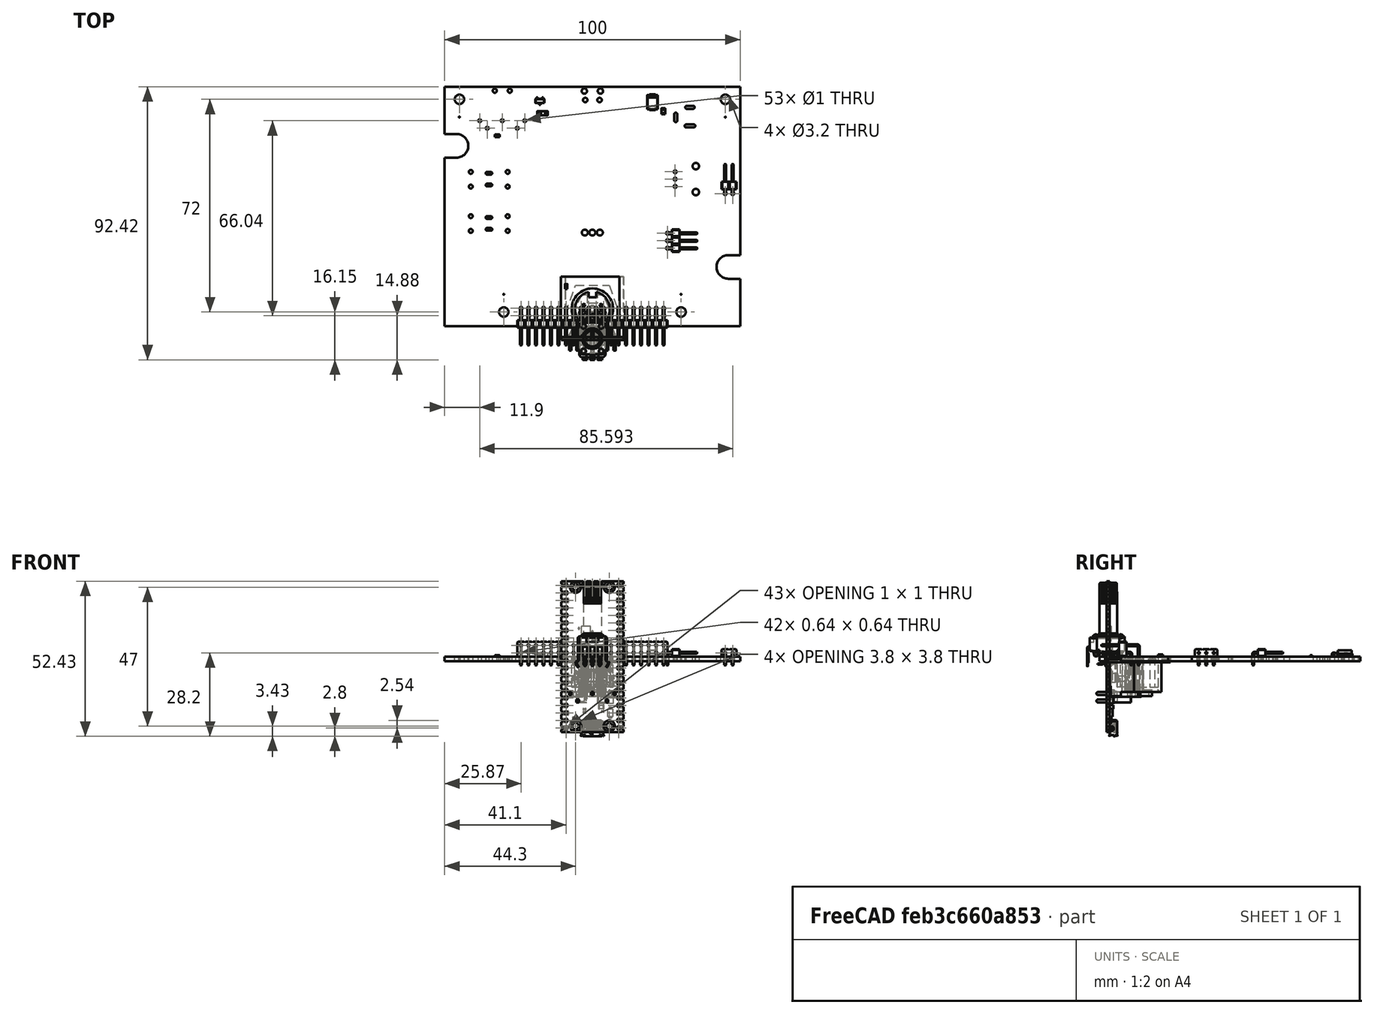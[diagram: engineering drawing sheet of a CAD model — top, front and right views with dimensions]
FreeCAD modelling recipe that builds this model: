
FCSTD DOCUMENT  (FreeCAD 0.21R33675 (Git))
Label: touch_keyboard_pcb
License: All rights reserved
LicenseURL: http://en.wikipedia.org/wiki/All_rights_reserved
objects: Part::Feature×161, App::Link×58, App::Part×42, PartDesign::CoordinateSystem×5, Sketcher::SketchObject×1
note: 167 computed .brp shape members not serialized (recipe doc carries the construction recipe); baked Part::Feature solids carry a one-line shape summary decoded from their .brp

FEATURE [PartDesign::CoordinateSystem] Local_CS_1056
  AttacherType = Attacher::AttachEngine3D
  MapMode = 2
  Support = -> [X_Axis001]
FEATURE [Part::Feature] Pcb_1056
  Placement = pos=(-142.24,138.54,0) rot=(0,0,1;0rad)
  shape: bbox 100 x 88.27 x 1.6 mm, 143 faces, 2 solids (baked)
FEATURE [Sketcher::SketchObject] PCB_Sketch_1056
  FullyConstrained = false
  sketch-geometry (16):
    g0: LineSegment StartX=46 StartY=20.27 StartZ=0 EndX=50 EndY=20.27 EndZ=0
    g1: LineSegment StartX=50 StartY=28.27 StartZ=0 EndX=46 EndY=28.27 EndZ=0
    g2: LineSegment StartX=-50 StartY=4.27 StartZ=0 EndX=-50 EndY=61.27 EndZ=0
    g3: LineSegment StartX=50 StartY=20.27 StartZ=0 EndX=50 EndY=4.27 EndZ=0
    g4: LineSegment StartX=50 StartY=85.27 StartZ=0 EndX=50 EndY=28.27 EndZ=0
    g5: LineSegment StartX=50 StartY=4.27 StartZ=0 EndX=-50 EndY=4.27 EndZ=0
    g6: LineSegment StartX=-50 StartY=85.27 StartZ=0 EndX=50 EndY=85.27 EndZ=0
    g7: LineSegment StartX=-46 StartY=69.27 StartZ=0 EndX=-50 EndY=69.27 EndZ=0
    g8: LineSegment StartX=-50 StartY=69.27 StartZ=0 EndX=-50 EndY=85.27 EndZ=0
    g9: LineSegment StartX=-50 StartY=61.27 StartZ=0 EndX=-46 EndY=61.27 EndZ=0
    g10: LineSegment StartX=-3 StartY=3 StartZ=0 EndX=3 EndY=3 EndZ=0
    g11: LineSegment StartX=3 StartY=3 StartZ=0 EndX=3 EndY=-3 EndZ=0
    g12: LineSegment StartX=3 StartY=-3 StartZ=0 EndX=-3 EndY=-3 EndZ=0
    g13: LineSegment StartX=-3 StartY=-3 StartZ=0 EndX=-3 EndY=3 EndZ=0
    g14: ArcOfCircle CenterX=-46 CenterY=65.27 CenterZ=0 NormalX=0 NormalY=0 NormalZ=-1 AngleXU=1.5708 Radius=4 StartAngle=0 EndAngle=3.14159
    g15: ArcOfCircle CenterX=46 CenterY=24.27 CenterZ=0 NormalX=0 NormalY=0 NormalZ=-1 AngleXU=-1.5708 Radius=4 StartAngle=0 EndAngle=3.14159
  constraints (16):
    c: Coincident(g2,g5)
    c: Coincident(g2,g9)
    c: Coincident(g7,g8)
    c: Coincident(g6,g8)
    c: Coincident(g9,g14)
    c: Coincident(g7,g14)
    c: Coincident(g12,g13)
    c: Coincident(g10,g13)
    c: Coincident(g11,g12)
    c: Coincident(g10,g11)
    c: Coincident(g0,g15)
    c: Coincident(g1,g15)
    c: Coincident(g3,g5)
    c: Coincident(g0,g3)
    c: Coincident(g1,g4)
    c: Coincident(g4,g6)
FEATURE [App::Part] Board_Geoms_1056
  Group = -> [Pcb_1056,PCB_Sketch_1056]
  Origin = -> Origin
FEATURE [Part::Feature] Shape  label="R33_R_0603_1608Metric_b52117b7a5b0"
  Placement = pos=(-32.195,68.69,0) rot=(0,0,1;0rad)
  shape: bbox 1.6 x 0.8 x 0.45 mm, 26 faces (baked)
FEATURE [Part::Feature] Shape001  label="C5_C_0603_1608Metric_656f8ebd2c8c"
  Placement = pos=(-8.89,17.65,0) rot=(0,0,-1;1.5708rad)
  shape: bbox 0.8 x 1.6 x 0.8 mm, 28 faces (baked)
FEATURE [App::Link] C5_C_0603_1608Metric_656f8ebd2c8c_ln_  label="C1_C_0603_1608Metric_563ebdbfda79"
  LinkPlacement = pos=(-19.05,17.65,0) rot=(0,0,-1;1.5708rad)
  LinkedObject = -> Shape001
  Placement = pos=(-19.05,17.65,0) rot=(0,0,-1;1.5708rad)
FEATURE [App::Link] R33_R_0603_1608Metric_b52117b7a5b0_ln_  label="R26_R_0603_1608Metric_01f404f3ffb8"
  LinkPlacement = pos=(11.43,13.89,0) rot=(0,0,-1;1.5708rad)
  LinkedObject = -> Shape
  Placement = pos=(11.43,13.89,0) rot=(0,0,-1;1.5708rad)
FEATURE [App::Link] R33_R_0603_1608Metric_b52117b7a5b0_ln_001  label="R29_R_0603_1608Metric_6abfc73d4d60"
  LinkPlacement = pos=(16.51,21.51,0) rot=(0,0,1;1.5708rad)
  LinkedObject = -> Shape
  Placement = pos=(16.51,21.51,0) rot=(0,0,1;1.5708rad)
FEATURE [App::Link] R33_R_0603_1608Metric_b52117b7a5b0_ln_002  label="R18_R_0603_1608Metric_edc7eae86286"
  LinkPlacement = pos=(1.27,13.89,0) rot=(0,0,-1;1.5708rad)
  LinkedObject = -> Shape
  Placement = pos=(1.27,13.89,0) rot=(0,0,-1;1.5708rad)
FEATURE [Part::Feature] Shape002  label="C18_C_0805_2012Metric_1ea8b0f87ad5"
  Placement = pos=(24,76.95,0) rot=(0,0,-1;1.5708rad)
  shape: bbox 1.25 x 2 x 1.25 mm, 28 faces (baked)
FEATURE [App::Link] R33_R_0603_1608Metric_b52117b7a5b0_ln_003  label="R8_R_0603_1608Metric_bf92398081f5"
  LinkPlacement = pos=(-11.43,13.89,0) rot=(0,0,-1;1.5708rad)
  LinkedObject = -> Shape
  Placement = pos=(-11.43,13.89,0) rot=(0,0,-1;1.5708rad)
FEATURE [App::Link] R33_R_0603_1608Metric_b52117b7a5b0_ln_004  label="R13_R_0603_1608Metric_2dbb6f5059f9"
  LinkPlacement = pos=(-3.81,21.51,0) rot=(0,0,1;1.5708rad)
  LinkedObject = -> Shape
  Placement = pos=(-3.81,21.51,0) rot=(0,0,1;1.5708rad)
FEATURE [App::Link] R33_R_0603_1608Metric_b52117b7a5b0_ln_005  label="R35_R_0603_1608Metric_a618b7082673"
  LinkPlacement = pos=(-15.685,83.93,0) rot=(0,0,1;3.14159rad)
  LinkedObject = -> Shape
  Placement = pos=(-15.685,83.93,0) rot=(0,0,1;3.14159rad)
FEATURE [App::Link] R33_R_0603_1608Metric_b52117b7a5b0_ln_006  label="R17_R_0603_1608Metric_51bdb2eb4169"
  LinkPlacement = pos=(1.27,21.51,0) rot=(0,0,1;1.5708rad)
  LinkedObject = -> Shape
  Placement = pos=(1.27,21.51,0) rot=(0,0,1;1.5708rad)
FEATURE [Part::Feature] Part__Feature  label="PCB, Raspberry Pi Pico-R3"
  shape: bbox 21 x 1 x 51 mm, 416 faces (baked)
FEATURE [Part::Feature] Part__Feature001  label="MicroUSB Port, Raspberry Pi Pico-R3"
  Placement = pos=(0,0.5,-24.35) rot=(0,1,0;3.14159rad)
  shape: bbox 7.999 x 2.949 x 5.461 mm, 809 faces (baked)
FEATURE [Part::Feature] Part__Feature002  label="MicroUSB Port, Raspberry Pi Pico-R004"
  Placement = pos=(0,0.5,-24.35) rot=(0,1,0;3.14159rad)
  shape: bbox 6.982 x 2.155 x 3.937 mm, 206 faces (baked)
FEATURE [Part::Feature] Part__Feature003  label="MicroUSB Port, Raspberry Pi Pico-R005"
  Placement = pos=(0,0.5,-24.35) rot=(0,1,0;3.14159rad)
  shape: bbox 0.37 x 1.716 x 4 mm, 43 faces (baked)
FEATURE [Part::Feature] Part__Feature004  label="MicroUSB Port, Raspberry Pi Pico-R006"
  Placement = pos=(0,0.5,-24.35) rot=(0,1,0;3.14159rad)
  shape: bbox 0.37 x 1.716 x 4 mm, 43 faces (baked)
FEATURE [Part::Feature] Part__Feature005  label="MicroUSB Port, Raspberry Pi Pico-R007"
  Placement = pos=(0,0.5,-24.35) rot=(0,1,0;3.14159rad)
  shape: bbox 0.37 x 1.716 x 4 mm, 43 faces (baked)
FEATURE [Part::Feature] Part__Feature006  label="MicroUSB Port, Raspberry Pi Pico-R008"
  Placement = pos=(0,0.5,-24.35) rot=(0,1,0;3.14159rad)
  shape: bbox 0.37 x 1.716 x 4 mm, 43 faces (baked)
FEATURE [Part::Feature] Part__Feature007  label="MicroUSB Port, Raspberry Pi Pico-R009"
  Placement = pos=(0,0.5,-24.35) rot=(0,1,0;3.14159rad)
  shape: bbox 0.37 x 1.716 x 4 mm, 43 faces (baked)
FEATURE [App::Part] MicroUSB_Port__Raspberry_Pi_Pico_R3  label="MicroUSB Port, Raspberry Pi Pico-R010"
  Group = -> [Part__Feature001,Part__Feature002,Part__Feature003,Part__Feature004,Part__Feature005,Part__Feature006,Part__Feature007]
  Origin = -> Origin008
FEATURE [Part::Feature] Part__Feature008  label="RP2040 Microcontroller, Raspberry Pi Pico-R3"
  Placement = pos=(0,0.5,0.5) rot=(0,0,1;0rad)
  shape: bbox 7 x 0.9 x 7 mm, 6 faces (baked)
FEATURE [Part::Feature] Part__Feature009  label="SW1, Tact Switch, Raspberry Pi Pico-R3"
  Placement = pos=(-3.5,0.5,-13.5) rot=(0,0,1;0rad)
  shape: bbox 3.2 x 2.5 x 4.25 mm, 17 faces (baked)
FEATURE [Part::Feature] Part__Feature010  label="D1, Diode, Schottky, Raspberry Pi Pico-R3"
  Placement = pos=(6,0.5,-19) rot=(0,0,1;0rad)
  shape: bbox 1.65 x 0.95 x 3.6 mm, 14 faces (baked)
FEATURE [Part::Feature] Part__Feature011  label="D2, QSME-C194, LED, Raspberry Pi Pico-R3"
  Placement = pos=(-5.8,0.5,-20.8) rot=(0,0,1;0rad)
  shape: bbox 1.6 x 0.55 x 0.8 mm, 6 faces (baked)
FEATURE [Part::Feature] Part__Feature012  label="L1, Inductor, Raspberry Pi Pico-R3"
  Placement = pos=(6,0.5,-14.6) rot=(0,0,1;0rad)
  shape: bbox 2 x 1.2 x 2.5 mm, 6 faces (baked)
FEATURE [Part::Feature] Part__Feature013  label="U2, RT6150B-33GQW, Buck Boost Converter, Raspberry Pi Pico-R3"
  Placement = pos=(3,0.5,-14.6) rot=(0,0,1;0rad)
  shape: bbox 2.5 x 0.8 x 2.5 mm, 6 faces (baked)
FEATURE [Part::Feature] Part__Feature014  label="U3, W25Q16JVUXIQ, Serial NOR Flash 16 Mbit, Raspberry Pi Pico-R3"
  Placement = pos=(-3.8,0.5,-6.4) rot=(0,0,1;0rad)
  shape: bbox 2 x 0.8 x 3 mm, 6 faces (baked)
FEATURE [Part::Feature] Part__Feature015  label="Q1, MOSFET, DMG1012T, Raspberry Pi Pico-R3"
  Placement = pos=(6.5,0.5,-7.2) rot=(0,0,1;0rad)
  shape: bbox 1.6 x 0.6 x 1.8 mm, 18 faces (baked)
FEATURE [Part::Feature] Part__Feature016  label="X1, X12M000000S096, 12 Mhz Crystal Resonator, Raspberry Pi Pico-R3"
  Placement = pos=(-2.2,0.5,9) rot=(0,0,1;0rad)
  shape: bbox 3.2 x 0.6 x 2.5 mm, 18 faces (baked)
FEATURE [Part::Feature] Part__Feature017  label="SMD Resistor, Configurable, Raspberry Pi Pico-R3_R1"
  Placement = pos=(6.2,0.5,1) rot=(0,1,0;1.5708rad)
  shape: bbox 0.6 x 0.35 x 0.5 mm, 6 faces (baked)
FEATURE [Part::Feature] Part__Feature018  label="SMD Resistor, Configurable, Raspberry Pi Pico-R3_R002"
  Placement = pos=(6.2,0.5,1) rot=(0,1,0;1.5708rad)
  shape: bbox 0.2 x 0.35 x 0.5 mm, 6 faces (baked)
FEATURE [Part::Feature] Part__Feature019  label="SMD Resistor, Configurable, Raspberry Pi Pico-R3_R003"
  Placement = pos=(6.2,0.5,1) rot=(0,1,0;1.5708rad)
  shape: bbox 0.2 x 0.35 x 0.5 mm, 6 faces (baked)
FEATURE [App::Part] SMD_Resistor__Configurable__Raspberry_Pi_Pico_R3_R1  label="SMD Resistor, Configurable, Raspberry Pi Pico-R3_R004"
  Group = -> [Part__Feature017,Part__Feature018,Part__Feature019]
  Origin = -> Origin009
FEATURE [Part::Feature] Part__Feature020  label="SMD Resistor, Configurable, Raspberry Pi Pico-R3_R2"
  Placement = pos=(3.5,0.5,-18.6) rot=(0,1,0;1.5708rad)
  shape: bbox 0.6 x 0.35 x 0.5 mm, 6 faces (baked)
FEATURE [Part::Feature] Part__Feature021  label="SMD Resistor, Configurable, Raspberry Pi Pico-R3_R005"
  Placement = pos=(3.5,0.5,-18.6) rot=(0,1,0;1.5708rad)
  shape: bbox 0.2 x 0.35 x 0.5 mm, 6 faces (baked)
FEATURE [Part::Feature] Part__Feature022  label="SMD Resistor, Configurable, Raspberry Pi Pico-R3_R006"
  Placement = pos=(3.5,0.5,-18.6) rot=(0,1,0;1.5708rad)
  shape: bbox 0.2 x 0.35 x 0.5 mm, 6 faces (baked)
FEATURE [App::Part] SMD_Resistor__Configurable__Raspberry_Pi_Pico_R3_R2  label="SMD Resistor, Configurable, Raspberry Pi Pico-R3_R007"
  Group = -> [Part__Feature020,Part__Feature021,Part__Feature022]
  Origin = -> Origin010
FEATURE [Part::Feature] Part__Feature023  label="SMD Resistor, Configurable, Raspberry Pi Pico-R3_R3"
  Placement = pos=(-2.7,0.5,-17.8) rot=(0,1,0;1.5708rad)
  shape: bbox 0.6 x 0.35 x 0.5 mm, 6 faces (baked)
FEATURE [Part::Feature] Part__Feature024  label="SMD Resistor, Configurable, Raspberry Pi Pico-R3_R008"
  Placement = pos=(-2.7,0.5,-17.8) rot=(0,1,0;1.5708rad)
  shape: bbox 0.2 x 0.35 x 0.5 mm, 6 faces (baked)
FEATURE [Part::Feature] Part__Feature025  label="SMD Resistor, Configurable, Raspberry Pi Pico-R3_R009"
  Placement = pos=(-2.7,0.5,-17.8) rot=(0,1,0;1.5708rad)
  shape: bbox 0.2 x 0.35 x 0.5 mm, 6 faces (baked)
FEATURE [App::Part] SMD_Resistor__Configurable__Raspberry_Pi_Pico_R3_R3  label="SMD Resistor, Configurable, Raspberry Pi Pico-R3_R010"
  Group = -> [Part__Feature023,Part__Feature024,Part__Feature025]
  Origin = -> Origin011
FEATURE [Part::Feature] Part__Feature026  label="SMD Resistor, Configurable, Raspberry Pi Pico-R3_R4"
  Placement = pos=(-5.5,0.5,-5.4) rot=(0,1,0;3.14159rad)
  shape: bbox 0.5 x 0.35 x 0.6 mm, 6 faces (baked)
FEATURE [Part::Feature] Part__Feature027  label="SMD Resistor, Configurable, Raspberry Pi Pico-R3_R011"
  Placement = pos=(-5.5,0.5,-5.4) rot=(0,1,0;3.14159rad)
  shape: bbox 0.5 x 0.35 x 0.2 mm, 6 faces (baked)
FEATURE [Part::Feature] Part__Feature028  label="SMD Resistor, Configurable, Raspberry Pi Pico-R3_R012"
  Placement = pos=(-5.5,0.5,-5.4) rot=(0,1,0;3.14159rad)
  shape: bbox 0.5 x 0.35 x 0.2 mm, 6 faces (baked)
FEATURE [App::Part] SMD_Resistor__Configurable__Raspberry_Pi_Pico_R3_R4  label="SMD Resistor, Configurable, Raspberry Pi Pico-R3_R013"
  Group = -> [Part__Feature026,Part__Feature027,Part__Feature028]
  Origin = -> Origin012
FEATURE [Part::Feature] Part__Feature029  label="SMD Resistor, Configurable, Raspberry Pi Pico-R3_R5"
  Placement = pos=(7,0.5,-9.6) rot=(0,1,0;3.14159rad)
  shape: bbox 0.5 x 0.35 x 0.6 mm, 6 faces (baked)
FEATURE [Part::Feature] Part__Feature030  label="SMD Resistor, Configurable, Raspberry Pi Pico-R3_R014"
  Placement = pos=(7,0.5,-9.6) rot=(0,1,0;3.14159rad)
  shape: bbox 0.5 x 0.35 x 0.2 mm, 6 faces (baked)
FEATURE [Part::Feature] Part__Feature031  label="SMD Resistor, Configurable, Raspberry Pi Pico-R3_R015"
  Placement = pos=(7,0.5,-9.6) rot=(0,1,0;3.14159rad)
  shape: bbox 0.5 x 0.35 x 0.2 mm, 6 faces (baked)
FEATURE [App::Part] SMD_Resistor__Configurable__Raspberry_Pi_Pico_R3_R5  label="SMD Resistor, Configurable, Raspberry Pi Pico-R3_R016"
  Group = -> [Part__Feature029,Part__Feature030,Part__Feature031]
  Origin = -> Origin013
FEATURE [Part::Feature] Part__Feature032  label="SMD Resistor, Configurable, Raspberry Pi Pico-R3_R6"
  Placement = pos=(6.5,0.5,-4.6) rot=(0,1,0;3.14159rad)
  shape: bbox 0.5 x 0.35 x 0.6 mm, 6 faces (baked)
FEATURE [Part::Feature] Part__Feature033  label="SMD Resistor, Configurable, Raspberry Pi Pico-R3_R017"
  Placement = pos=(6.5,0.5,-4.6) rot=(0,1,0;3.14159rad)
  shape: bbox 0.5 x 0.35 x 0.2 mm, 6 faces (baked)
FEATURE [Part::Feature] Part__Feature034  label="SMD Resistor, Configurable, Raspberry Pi Pico-R3_R018"
  Placement = pos=(6.5,0.5,-4.6) rot=(0,1,0;3.14159rad)
  shape: bbox 0.5 x 0.35 x 0.2 mm, 6 faces (baked)
FEATURE [App::Part] SMD_Resistor__Configurable__Raspberry_Pi_Pico_R3_R6  label="SMD Resistor, Configurable, Raspberry Pi Pico-R3_R019"
  Group = -> [Part__Feature032,Part__Feature033,Part__Feature034]
  Origin = -> Origin014
FEATURE [Part::Feature] Part__Feature035  label="SMD Resistor, Configurable, Raspberry Pi Pico-R3_R7"
  Placement = pos=(4.5,0.5,-9) rot=(0,1,0;3.14159rad)
  shape: bbox 0.8 x 0.45 x 1 mm, 6 faces (baked)
FEATURE [Part::Feature] Part__Feature036  label="SMD Resistor, Configurable, Raspberry Pi Pico-R3_R020"
  Placement = pos=(4.5,0.5,-9) rot=(0,1,0;3.14159rad)
  shape: bbox 0.8 x 0.45 x 0.3 mm, 6 faces (baked)
FEATURE [Part::Feature] Part__Feature037  label="SMD Resistor, Configurable, Raspberry Pi Pico-R3_R021"
  Placement = pos=(4.5,0.5,-9) rot=(0,1,0;3.14159rad)
  shape: bbox 0.8 x 0.45 x 0.3 mm, 6 faces (baked)
FEATURE [App::Part] SMD_Resistor__Configurable__Raspberry_Pi_Pico_R3_R7  label="SMD Resistor, Configurable, Raspberry Pi Pico-R3_R022"
  Group = -> [Part__Feature035,Part__Feature036,Part__Feature037]
  Origin = -> Origin015
FEATURE [Part::Feature] Part__Feature038  label="SMD Resistor, Configurable, Raspberry Pi Pico-R3_R8"
  Placement = pos=(-2.7,0.5,-18.8) rot=(0,1,0;1.5708rad)
  shape: bbox 0.6 x 0.35 x 0.5 mm, 6 faces (baked)
FEATURE [Part::Feature] Part__Feature039  label="SMD Resistor, Configurable, Raspberry Pi Pico-R3_R023"
  Placement = pos=(-2.7,0.5,-18.8) rot=(0,1,0;1.5708rad)
  shape: bbox 0.2 x 0.35 x 0.5 mm, 6 faces (baked)
FEATURE [Part::Feature] Part__Feature040  label="SMD Resistor, Configurable, Raspberry Pi Pico-R3_R024"
  Placement = pos=(-2.7,0.5,-18.8) rot=(0,1,0;1.5708rad)
  shape: bbox 0.2 x 0.35 x 0.5 mm, 6 faces (baked)
FEATURE [App::Part] SMD_Resistor__Configurable__Raspberry_Pi_Pico_R3_R8  label="SMD Resistor, Configurable, Raspberry Pi Pico-R3_R025"
  Group = -> [Part__Feature038,Part__Feature039,Part__Feature040]
  Origin = -> Origin016
FEATURE [Part::Feature] Part__Feature041  label="SMD Resistor, Configurable, Raspberry Pi Pico-R3_R9"
  Placement = pos=(5.5,0.5,-4.6) rot=(0,1,0;3.14159rad)
  shape: bbox 0.5 x 0.35 x 0.6 mm, 6 faces (baked)
FEATURE [Part::Feature] Part__Feature042  label="SMD Resistor, Configurable, Raspberry Pi Pico-R3_R026"
  Placement = pos=(5.5,0.5,-4.6) rot=(0,1,0;3.14159rad)
  shape: bbox 0.5 x 0.35 x 0.2 mm, 6 faces (baked)
FEATURE [Part::Feature] Part__Feature043  label="SMD Resistor, Configurable, Raspberry Pi Pico-R3_R027"
  Placement = pos=(5.5,0.5,-4.6) rot=(0,1,0;3.14159rad)
  shape: bbox 0.5 x 0.35 x 0.2 mm, 6 faces (baked)
FEATURE [App::Part] SMD_Resistor__Configurable__Raspberry_Pi_Pico_R3_R9  label="SMD Resistor, Configurable, Raspberry Pi Pico-R3_R028"
  Group = -> [Part__Feature041,Part__Feature042,Part__Feature043]
  Origin = -> Origin017
FEATURE [Part::Feature] Part__Feature044  label="SMD Resistor, Configurable, Raspberry Pi Pico-R3_R10"
  Placement = pos=(6.2,0.5,-1e-16) rot=(0,1,0;1.5708rad)
  shape: bbox 0.6 x 0.35 x 0.5 mm, 6 faces (baked)
FEATURE [Part::Feature] Part__Feature045  label="SMD Resistor, Configurable, Raspberry Pi Pico-R3_R029"
  Placement = pos=(6.2,0.5,-1e-16) rot=(0,1,0;1.5708rad)
  shape: bbox 0.2 x 0.35 x 0.5 mm, 6 faces (baked)
FEATURE [Part::Feature] Part__Feature046  label="SMD Resistor, Configurable, Raspberry Pi Pico-R3_R030"
  Placement = pos=(6.2,0.5,-1e-16) rot=(0,1,0;1.5708rad)
  shape: bbox 0.2 x 0.35 x 0.5 mm, 6 faces (baked)
FEATURE [App::Part] SMD_Resistor__Configurable__Raspberry_Pi_Pico_R3_R10  label="SMD Resistor, Configurable, Raspberry Pi Pico-R3_R031"
  Group = -> [Part__Feature044,Part__Feature045,Part__Feature046]
  Origin = -> Origin018
FEATURE [Part::Feature] Part__Feature047  label="SMD Resistor, Configurable, Raspberry Pi Pico-R3_R11"
  Placement = pos=(-5.5,0.5,-7.4) rot=(0,0,1;0rad)
  shape: bbox 0.5 x 0.35 x 0.6 mm, 6 faces (baked)
FEATURE [Part::Feature] Part__Feature048  label="SMD Resistor, Configurable, Raspberry Pi Pico-R3_R032"
  Placement = pos=(-5.5,0.5,-7.4) rot=(0,0,1;0rad)
  shape: bbox 0.5 x 0.35 x 0.2 mm, 6 faces (baked)
FEATURE [Part::Feature] Part__Feature049  label="SMD Resistor, Configurable, Raspberry Pi Pico-R3_R033"
  Placement = pos=(-5.5,0.5,-7.4) rot=(0,0,1;0rad)
  shape: bbox 0.5 x 0.35 x 0.2 mm, 6 faces (baked)
FEATURE [App::Part] SMD_Resistor__Configurable__Raspberry_Pi_Pico_R3_R11  label="SMD Resistor, Configurable, Raspberry Pi Pico-R3_R034"
  Group = -> [Part__Feature047,Part__Feature048,Part__Feature049]
  Origin = -> Origin019
FEATURE [Part::Feature] Part__Feature050  label="SMD Resistor, Configurable, Raspberry Pi Pico-R3_R12"
  Placement = pos=(0.8,0.5,-4.6) rot=(0,1,0;3.14159rad)
  shape: bbox 0.3 x 0.23 x 0.4 mm, 6 faces (baked)
FEATURE [Part::Feature] Part__Feature051  label="SMD Resistor, Configurable, Raspberry Pi Pico-R3_R035"
  Placement = pos=(0.8,0.5,-4.6) rot=(0,1,0;3.14159rad)
  shape: bbox 0.3 x 0.23 x 0.1 mm, 6 faces (baked)
FEATURE [Part::Feature] Part__Feature052  label="SMD Resistor, Configurable, Raspberry Pi Pico-R3_R036"
  Placement = pos=(0.8,0.5,-4.6) rot=(0,1,0;3.14159rad)
  shape: bbox 0.3 x 0.23 x 0.1 mm, 6 faces (baked)
FEATURE [App::Part] SMD_Resistor__Configurable__Raspberry_Pi_Pico_R3_R12  label="SMD Resistor, Configurable, Raspberry Pi Pico-R3_R037"
  Group = -> [Part__Feature050,Part__Feature051,Part__Feature052]
  Origin = -> Origin020
FEATURE [Part::Feature] Part__Feature053  label="SMD Resistor, Configurable, Raspberry Pi Pico-R3_R13"
  Placement = pos=(1.4,0.5,-4.6) rot=(0,1,0;3.14159rad)
  shape: bbox 0.3 x 0.23 x 0.4 mm, 6 faces (baked)
FEATURE [Part::Feature] Part__Feature054  label="SMD Resistor, Configurable, Raspberry Pi Pico-R3_R038"
  Placement = pos=(1.4,0.5,-4.6) rot=(0,1,0;3.14159rad)
  shape: bbox 0.3 x 0.23 x 0.1 mm, 6 faces (baked)
FEATURE [Part::Feature] Part__Feature055  label="SMD Resistor, Configurable, Raspberry Pi Pico-R3_R039"
  Placement = pos=(1.4,0.5,-4.6) rot=(0,1,0;3.14159rad)
  shape: bbox 0.3 x 0.23 x 0.1 mm, 6 faces (baked)
FEATURE [App::Part] SMD_Resistor__Configurable__Raspberry_Pi_Pico_R3_R13  label="SMD Resistor, Configurable, Raspberry Pi Pico-R3_R040"
  Group = -> [Part__Feature053,Part__Feature054,Part__Feature055]
  Origin = -> Origin021
FEATURE [Part::Feature] Part__Feature056  label="SMD Resistor, Configurable, Raspberry Pi Pico-R3_R14"
  Placement = pos=(-1.1,0.5,7) rot=(0,1,0;1.5708rad)
  shape: bbox 0.6 x 0.35 x 0.5 mm, 6 faces (baked)
FEATURE [Part::Feature] Part__Feature057  label="SMD Resistor, Configurable, Raspberry Pi Pico-R3_R041"
  Placement = pos=(-1.1,0.5,7) rot=(0,1,0;1.5708rad)
  shape: bbox 0.2 x 0.35 x 0.5 mm, 6 faces (baked)
FEATURE [Part::Feature] Part__Feature058  label="SMD Resistor, Configurable, Raspberry Pi Pico-R3_R042"
  Placement = pos=(-1.1,0.5,7) rot=(0,1,0;1.5708rad)
  shape: bbox 0.2 x 0.35 x 0.5 mm, 6 faces (baked)
FEATURE [App::Part] SMD_Resistor__Configurable__Raspberry_Pi_Pico_R3_R14  label="SMD Resistor, Configurable, Raspberry Pi Pico-R3_R043"
  Group = -> [Part__Feature056,Part__Feature057,Part__Feature058]
  Origin = -> Origin022
FEATURE [Part::Feature] Part__Feature059  label="SMD Resistor, Configurable, Raspberry Pi Pico-R3_R15"
  Placement = pos=(-1.7,0.5,6.2) rot=(0,1,0;1.5708rad)
  shape: bbox 0.6 x 0.35 x 0.5 mm, 6 faces (baked)
FEATURE [Part::Feature] Part__Feature060  label="SMD Resistor, Configurable, Raspberry Pi Pico-R3_R044"
  Placement = pos=(-1.7,0.5,6.2) rot=(0,1,0;1.5708rad)
  shape: bbox 0.2 x 0.35 x 0.5 mm, 6 faces (baked)
FEATURE [Part::Feature] Part__Feature061  label="SMD Resistor, Configurable, Raspberry Pi Pico-R3_R045"
  Placement = pos=(-1.7,0.5,6.2) rot=(0,1,0;1.5708rad)
  shape: bbox 0.2 x 0.35 x 0.5 mm, 6 faces (baked)
FEATURE [App::Part] SMD_Resistor__Configurable__Raspberry_Pi_Pico_R3_R15  label="SMD Resistor, Configurable, Raspberry Pi Pico-R3_R046"
  Group = -> [Part__Feature059,Part__Feature060,Part__Feature061]
  Origin = -> Origin023
FEATURE [Part::Feature] Part__Feature062  label="SMD Capacitor, Configurable, Raspberry Pi Pico-R3_C1"
  Placement = pos=(3,0.5,-17) rot=(0,1,0;1.5708rad)
  shape: bbox 1.2 x 1.25 x 1.25 mm, 6 faces (baked)
FEATURE [Part::Feature] Part__Feature063  label="SMD Capacitor, Configurable, Raspberry Pi Pico-R3_C002"
  Placement = pos=(3,0.5,-17) rot=(0,1,0;1.5708rad)
  shape: bbox 0.4 x 1.25 x 1.25 mm, 6 faces (baked)
FEATURE [Part::Feature] Part__Feature064  label="SMD Capacitor, Configurable, Raspberry Pi Pico-R3_C003"
  Placement = pos=(3,0.5,-17) rot=(0,1,0;1.5708rad)
  shape: bbox 0.4 x 1.25 x 1.25 mm, 6 faces (baked)
FEATURE [App::Part] SMD_Capacitor__Configurable__Raspberry_Pi_Pico_R3_C1  label="SMD Capacitor, Configurable, Raspberry Pi Pico-R3_C004"
  Group = -> [Part__Feature062,Part__Feature063,Part__Feature064]
  Origin = -> Origin024
FEATURE [Part::Feature] Part__Feature065  label="SMD Capacitor, Configurable, Raspberry Pi Pico-R3_C2"
  Placement = pos=(3,0.5,-12) rot=(0,1,0;1.5708rad)
  shape: bbox 1.2 x 1.25 x 1.25 mm, 6 faces (baked)
FEATURE [Part::Feature] Part__Feature066  label="SMD Capacitor, Configurable, Raspberry Pi Pico-R3_C005"
  Placement = pos=(3,0.5,-12) rot=(0,1,0;1.5708rad)
  shape: bbox 0.4 x 1.25 x 1.25 mm, 6 faces (baked)
FEATURE [Part::Feature] Part__Feature067  label="SMD Capacitor, Configurable, Raspberry Pi Pico-R3_C006"
  Placement = pos=(3,0.5,-12) rot=(0,1,0;1.5708rad)
  shape: bbox 0.4 x 1.25 x 1.25 mm, 6 faces (baked)
FEATURE [App::Part] SMD_Capacitor__Configurable__Raspberry_Pi_Pico_R3_C2  label="SMD Capacitor, Configurable, Raspberry Pi Pico-R3_C007"
  Group = -> [Part__Feature065,Part__Feature066,Part__Feature067]
  Origin = -> Origin025
FEATURE [Part::Feature] Part__Feature068  label="SMD Capacitor, Configurable, Raspberry Pi Pico-R3_C3"
  Placement = pos=(6,0.5,-9.4) rot=(0,0,1;0rad)
  shape: bbox 0.3 x 0.3 x 0.4 mm, 6 faces (baked)
FEATURE [Part::Feature] Part__Feature069  label="SMD Capacitor, Configurable, Raspberry Pi Pico-R3_C008"
  Placement = pos=(6,0.5,-9.4) rot=(0,0,1;0rad)
  shape: bbox 0.3 x 0.3 x 0.1 mm, 6 faces (baked)
FEATURE [Part::Feature] Part__Feature070  label="SMD Capacitor, Configurable, Raspberry Pi Pico-R3_C009"
  Placement = pos=(6,0.5,-9.4) rot=(0,0,1;0rad)
  shape: bbox 0.3 x 0.3 x 0.1 mm, 6 faces (baked)
FEATURE [App::Part] SMD_Capacitor__Configurable__Raspberry_Pi_Pico_R3_C3  label="SMD Capacitor, Configurable, Raspberry Pi Pico-R3_C010"
  Group = -> [Part__Feature068,Part__Feature069,Part__Feature070]
  Origin = -> Origin026
FEATURE [Part::Feature] Part__Feature071  label="SMD Capacitor, Configurable, Raspberry Pi Pico-R3_C4"
  Placement = pos=(-4.5,0.5,-2.1) rot=(0,-1,0;1.5708rad)
  shape: bbox 0.4 x 0.3 x 0.3 mm, 6 faces (baked)
FEATURE [Part::Feature] Part__Feature072  label="SMD Capacitor, Configurable, Raspberry Pi Pico-R3_C011"
  Placement = pos=(-4.5,0.5,-2.1) rot=(0,-1,0;1.5708rad)
  shape: bbox 0.1 x 0.3 x 0.3 mm, 6 faces (baked)
FEATURE [Part::Feature] Part__Feature073  label="SMD Capacitor, Configurable, Raspberry Pi Pico-R3_C012"
  Placement = pos=(-4.5,0.5,-2.1) rot=(0,-1,0;1.5708rad)
  shape: bbox 0.1 x 0.3 x 0.3 mm, 6 faces (baked)
FEATURE [App::Part] SMD_Capacitor__Configurable__Raspberry_Pi_Pico_R3_C4  label="SMD Capacitor, Configurable, Raspberry Pi Pico-R3_C013"
  Group = -> [Part__Feature071,Part__Feature072,Part__Feature073]
  Origin = -> Origin027
FEATURE [Part::Feature] Part__Feature074  label="SMD Capacitor, Configurable, Raspberry Pi Pico-R3_C5"
  Placement = pos=(-4.5,0.5,1.5) rot=(0,-1,0;1.5708rad)
  shape: bbox 0.4 x 0.3 x 0.3 mm, 6 faces (baked)
FEATURE [Part::Feature] Part__Feature075  label="SMD Capacitor, Configurable, Raspberry Pi Pico-R3_C014"
  Placement = pos=(-4.5,0.5,1.5) rot=(0,-1,0;1.5708rad)
  shape: bbox 0.1 x 0.3 x 0.3 mm, 6 faces (baked)
FEATURE [Part::Feature] Part__Feature076  label="SMD Capacitor, Configurable, Raspberry Pi Pico-R3_C015"
  Placement = pos=(-4.5,0.5,1.5) rot=(0,-1,0;1.5708rad)
  shape: bbox 0.1 x 0.3 x 0.3 mm, 6 faces (baked)
FEATURE [App::Part] SMD_Capacitor__Configurable__Raspberry_Pi_Pico_R3_C5  label="SMD Capacitor, Configurable, Raspberry Pi Pico-R3_C016"
  Group = -> [Part__Feature074,Part__Feature075,Part__Feature076]
  Origin = -> Origin028
FEATURE [Part::Feature] Part__Feature077  label="SMD Capacitor, Configurable, Raspberry Pi Pico-R3_C6"
  Placement = pos=(4.6,0.5,1.9) rot=(0,1,0;0.785398rad)
  shape: bbox 0.495 x 0.3 x 0.495 mm, 6 faces (baked)
FEATURE [Part::Feature] Part__Feature078  label="SMD Capacitor, Configurable, Raspberry Pi Pico-R3_C017"
  Placement = pos=(4.6,0.5,1.9) rot=(0,1,0;0.785398rad)
  shape: bbox 0.2828 x 0.3 x 0.2828 mm, 6 faces (baked)
FEATURE [Part::Feature] Part__Feature079  label="SMD Capacitor, Configurable, Raspberry Pi Pico-R3_C018"
  Placement = pos=(4.6,0.5,1.9) rot=(0,1,0;0.785398rad)
  shape: bbox 0.2828 x 0.3 x 0.2828 mm, 6 faces (baked)
FEATURE [App::Part] SMD_Capacitor__Configurable__Raspberry_Pi_Pico_R3_C6  label="SMD Capacitor, Configurable, Raspberry Pi Pico-R3_C019"
  Group = -> [Part__Feature077,Part__Feature078,Part__Feature079]
  Origin = -> Origin029
FEATURE [Part::Feature] Part__Feature080  label="SMD Capacitor, Configurable, Raspberry Pi Pico-R3_C7"
  Placement = pos=(4.5,0.5,-2.4) rot=(0,-1,0;1.5708rad)
  shape: bbox 0.4 x 0.3 x 0.3 mm, 6 faces (baked)
FEATURE [Part::Feature] Part__Feature081  label="SMD Capacitor, Configurable, Raspberry Pi Pico-R3_C020"
  Placement = pos=(4.5,0.5,-2.4) rot=(0,-1,0;1.5708rad)
  shape: bbox 0.1 x 0.3 x 0.3 mm, 6 faces (baked)
FEATURE [Part::Feature] Part__Feature082  label="SMD Capacitor, Configurable, Raspberry Pi Pico-R3_C021"
  Placement = pos=(4.5,0.5,-2.4) rot=(0,-1,0;1.5708rad)
  shape: bbox 0.1 x 0.3 x 0.3 mm, 6 faces (baked)
FEATURE [App::Part] SMD_Capacitor__Configurable__Raspberry_Pi_Pico_R3_C7  label="SMD Capacitor, Configurable, Raspberry Pi Pico-R3_C022"
  Group = -> [Part__Feature080,Part__Feature081,Part__Feature082]
  Origin = -> Origin030
FEATURE [Part::Feature] Part__Feature083  label="SMD Capacitor, Configurable, Raspberry Pi Pico-R3_C8"
  Placement = pos=(0,0.5,5.5) rot=(0,0,1;0rad)
  shape: bbox 0.3 x 0.3 x 0.4 mm, 6 faces (baked)
FEATURE [Part::Feature] Part__Feature084  label="SMD Capacitor, Configurable, Raspberry Pi Pico-R3_C023"
  Placement = pos=(0,0.5,5.5) rot=(0,0,1;0rad)
  shape: bbox 0.3 x 0.3 x 0.1 mm, 6 faces (baked)
FEATURE [Part::Feature] Part__Feature085  label="SMD Capacitor, Configurable, Raspberry Pi Pico-R3_C024"
  Placement = pos=(0,0.5,5.5) rot=(0,0,1;0rad)
  shape: bbox 0.3 x 0.3 x 0.1 mm, 6 faces (baked)
FEATURE [App::Part] SMD_Capacitor__Configurable__Raspberry_Pi_Pico_R3_C8  label="SMD Capacitor, Configurable, Raspberry Pi Pico-R3_C025"
  Group = -> [Part__Feature083,Part__Feature084,Part__Feature085]
  Origin = -> Origin031
FEATURE [Part::Feature] Part__Feature086  label="SMD Capacitor, Configurable, Raspberry Pi Pico-R3_C9"
  Placement = pos=(0.8,0.5,5.5) rot=(0,0,1;0rad)
  shape: bbox 0.3 x 0.3 x 0.4 mm, 6 faces (baked)
FEATURE [Part::Feature] Part__Feature087  label="SMD Capacitor, Configurable, Raspberry Pi Pico-R3_C026"
  Placement = pos=(0.8,0.5,5.5) rot=(0,0,1;0rad)
  shape: bbox 0.3 x 0.3 x 0.1 mm, 6 faces (baked)
FEATURE [Part::Feature] Part__Feature088  label="SMD Capacitor, Configurable, Raspberry Pi Pico-R3_C027"
  Placement = pos=(0.8,0.5,5.5) rot=(0,0,1;0rad)
  shape: bbox 0.3 x 0.3 x 0.1 mm, 6 faces (baked)
FEATURE [App::Part] SMD_Capacitor__Configurable__Raspberry_Pi_Pico_R3_C9  label="SMD Capacitor, Configurable, Raspberry Pi Pico-R3_C028"
  Group = -> [Part__Feature086,Part__Feature087,Part__Feature088]
  Origin = -> Origin032
FEATURE [Part::Feature] Part__Feature089  label="SMD Capacitor, Configurable, Raspberry Pi Pico-R3_C10"
  Placement = pos=(0,0.5,-4.6) rot=(0,0,1;0rad)
  shape: bbox 0.3 x 0.3 x 0.4 mm, 6 faces (baked)
FEATURE [Part::Feature] Part__Feature090  label="SMD Capacitor, Configurable, Raspberry Pi Pico-R3_C029"
  Placement = pos=(0,0.5,-4.6) rot=(0,0,1;0rad)
  shape: bbox 0.3 x 0.3 x 0.1 mm, 6 faces (baked)
FEATURE [Part::Feature] Part__Feature091  label="SMD Capacitor, Configurable, Raspberry Pi Pico-R3_C030"
  Placement = pos=(0,0.5,-4.6) rot=(0,0,1;0rad)
  shape: bbox 0.3 x 0.3 x 0.1 mm, 6 faces (baked)
FEATURE [App::Part] SMD_Capacitor__Configurable__Raspberry_Pi_Pico_R3_C10  label="SMD Capacitor, Configurable, Raspberry Pi Pico-R3_C031"
  Group = -> [Part__Feature089,Part__Feature090,Part__Feature091]
  Origin = -> Origin033
FEATURE [Part::Feature] Part__Feature092  label="SMD Capacitor, Configurable, Raspberry Pi Pico-R3_C11"
  Placement = pos=(-0.7,0.5,-4.6) rot=(0,0,1;0rad)
  shape: bbox 0.3 x 0.3 x 0.4 mm, 6 faces (baked)
FEATURE [Part::Feature] Part__Feature093  label="SMD Capacitor, Configurable, Raspberry Pi Pico-R3_C032"
  Placement = pos=(-0.7,0.5,-4.6) rot=(0,0,1;0rad)
  shape: bbox 0.3 x 0.3 x 0.1 mm, 6 faces (baked)
FEATURE [Part::Feature] Part__Feature094  label="SMD Capacitor, Configurable, Raspberry Pi Pico-R3_C033"
  Placement = pos=(-0.7,0.5,-4.6) rot=(0,0,1;0rad)
  shape: bbox 0.3 x 0.3 x 0.1 mm, 6 faces (baked)
FEATURE [App::Part] SMD_Capacitor__Configurable__Raspberry_Pi_Pico_R3_C11  label="SMD Capacitor, Configurable, Raspberry Pi Pico-R3_C034"
  Group = -> [Part__Feature092,Part__Feature093,Part__Feature094]
  Origin = -> Origin034
FEATURE [Part::Feature] Part__Feature095  label="SMD Capacitor, Configurable, Raspberry Pi Pico-R3_C12"
  Placement = pos=(2.2,0.5,-4.6) rot=(0,0,1;0rad)
  shape: bbox 0.5 x 0.5 x 0.6 mm, 6 faces (baked)
FEATURE [Part::Feature] Part__Feature096  label="SMD Capacitor, Configurable, Raspberry Pi Pico-R3_C035"
  Placement = pos=(2.2,0.5,-4.6) rot=(0,0,1;0rad)
  shape: bbox 0.5 x 0.5 x 0.2 mm, 6 faces (baked)
FEATURE [Part::Feature] Part__Feature097  label="SMD Capacitor, Configurable, Raspberry Pi Pico-R3_C036"
  Placement = pos=(2.2,0.5,-4.6) rot=(0,0,1;0rad)
  shape: bbox 0.5 x 0.5 x 0.2 mm, 6 faces (baked)
FEATURE [App::Part] SMD_Capacitor__Configurable__Raspberry_Pi_Pico_R3_C12  label="SMD Capacitor, Configurable, Raspberry Pi Pico-R3_C037"
  Group = -> [Part__Feature095,Part__Feature096,Part__Feature097]
  Origin = -> Origin035
FEATURE [Part::Feature] Part__Feature098  label="SMD Capacitor, Configurable, Raspberry Pi Pico-R3_C13"
  Placement = pos=(4.6,0.5,-4.6) rot=(0,0,1;0rad)
  shape: bbox 0.5 x 0.5 x 0.6 mm, 6 faces (baked)
FEATURE [Part::Feature] Part__Feature099  label="SMD Capacitor, Configurable, Raspberry Pi Pico-R3_C038"
  Placement = pos=(4.6,0.5,-4.6) rot=(0,0,1;0rad)
  shape: bbox 0.5 x 0.5 x 0.2 mm, 6 faces (baked)
FEATURE [Part::Feature] Part__Feature100  label="SMD Capacitor, Configurable, Raspberry Pi Pico-R3_C039"
  Placement = pos=(4.6,0.5,-4.6) rot=(0,0,1;0rad)
  shape: bbox 0.5 x 0.5 x 0.2 mm, 6 faces (baked)
FEATURE [App::Part] SMD_Capacitor__Configurable__Raspberry_Pi_Pico_R3_C13  label="SMD Capacitor, Configurable, Raspberry Pi Pico-R3_C040"
  Group = -> [Part__Feature098,Part__Feature099,Part__Feature100]
  Origin = -> Origin036
FEATURE [Part::Feature] Part__Feature101  label="SMD Capacitor, Configurable, Raspberry Pi Pico-R3_C14"
  Placement = pos=(3.2,0.5,-4.6) rot=(0,0,1;0rad)
  shape: bbox 0.5 x 0.5 x 0.6 mm, 6 faces (baked)
FEATURE [Part::Feature] Part__Feature102  label="SMD Capacitor, Configurable, Raspberry Pi Pico-R3_C041"
  Placement = pos=(3.2,0.5,-4.6) rot=(0,0,1;0rad)
  shape: bbox 0.5 x 0.5 x 0.2 mm, 6 faces (baked)
FEATURE [Part::Feature] Part__Feature103  label="SMD Capacitor, Configurable, Raspberry Pi Pico-R3_C042"
  Placement = pos=(3.2,0.5,-4.6) rot=(0,0,1;0rad)
  shape: bbox 0.5 x 0.5 x 0.2 mm, 6 faces (baked)
FEATURE [App::Part] SMD_Capacitor__Configurable__Raspberry_Pi_Pico_R3_C14  label="SMD Capacitor, Configurable, Raspberry Pi Pico-R3_C043"
  Group = -> [Part__Feature101,Part__Feature102,Part__Feature103]
  Origin = -> Origin037
FEATURE [Part::Feature] Part__Feature104  label="SMD Capacitor, Configurable, Raspberry Pi Pico-R3_C15"
  Placement = pos=(-4.5,0.5,-8.8) rot=(0,0,1;0rad)
  shape: bbox 0.3 x 0.3 x 0.4 mm, 6 faces (baked)
FEATURE [Part::Feature] Part__Feature105  label="SMD Capacitor, Configurable, Raspberry Pi Pico-R3_C044"
  Placement = pos=(-4.5,0.5,-8.8) rot=(0,0,1;0rad)
  shape: bbox 0.3 x 0.3 x 0.1 mm, 6 faces (baked)
FEATURE [Part::Feature] Part__Feature106  label="SMD Capacitor, Configurable, Raspberry Pi Pico-R3_C045"
  Placement = pos=(-4.5,0.5,-8.8) rot=(0,0,1;0rad)
  shape: bbox 0.3 x 0.3 x 0.1 mm, 6 faces (baked)
FEATURE [App::Part] SMD_Capacitor__Configurable__Raspberry_Pi_Pico_R3_C15  label="SMD Capacitor, Configurable, Raspberry Pi Pico-R3_C046"
  Group = -> [Part__Feature104,Part__Feature105,Part__Feature106]
  Origin = -> Origin038
FEATURE [Part::Feature] Part__Feature107  label="SMD Capacitor, Configurable, Raspberry Pi Pico-R3_C16"
  Placement = pos=(-4.6,0.5,9.6) rot=(0,0,1;0rad)
  shape: bbox 0.3 x 0.3 x 0.4 mm, 6 faces (baked)
FEATURE [Part::Feature] Part__Feature108  label="SMD Capacitor, Configurable, Raspberry Pi Pico-R3_C047"
  Placement = pos=(-4.6,0.5,9.6) rot=(0,0,1;0rad)
  shape: bbox 0.3 x 0.3 x 0.1 mm, 6 faces (baked)
FEATURE [Part::Feature] Part__Feature109  label="SMD Capacitor, Configurable, Raspberry Pi Pico-R3_C048"
  Placement = pos=(-4.6,0.5,9.6) rot=(0,0,1;0rad)
  shape: bbox 0.3 x 0.3 x 0.1 mm, 6 faces (baked)
FEATURE [App::Part] SMD_Capacitor__Configurable__Raspberry_Pi_Pico_R3_C16  label="SMD Capacitor, Configurable, Raspberry Pi Pico-R3_C049"
  Group = -> [Part__Feature107,Part__Feature108,Part__Feature109]
  Origin = -> Origin039
FEATURE [Part::Feature] Part__Feature110  label="SMD Capacitor, Configurable, Raspberry Pi Pico-R3_C17"
  Placement = pos=(0,0.5,8.5) rot=(0,0,1;0rad)
  shape: bbox 0.3 x 0.3 x 0.4 mm, 6 faces (baked)
FEATURE [Part::Feature] Part__Feature111  label="SMD Capacitor, Configurable, Raspberry Pi Pico-R3_C050"
  Placement = pos=(0,0.5,8.5) rot=(0,0,1;0rad)
  shape: bbox 0.3 x 0.3 x 0.1 mm, 6 faces (baked)
FEATURE [Part::Feature] Part__Feature112  label="SMD Capacitor, Configurable, Raspberry Pi Pico-R3_C051"
  Placement = pos=(0,0.5,8.5) rot=(0,0,1;0rad)
  shape: bbox 0.3 x 0.3 x 0.1 mm, 6 faces (baked)
FEATURE [App::Part] SMD_Capacitor__Configurable__Raspberry_Pi_Pico_R3_C17  label="SMD Capacitor, Configurable, Raspberry Pi Pico-R3_C052"
  Group = -> [Part__Feature110,Part__Feature111,Part__Feature112]
  Origin = -> Origin040
FEATURE [Part::Feature] Part__Feature113  label="SMD Capacitor, Configurable, Raspberry Pi Pico-R3_C18"
  Placement = pos=(-4.7,0.5,-3.1) rot=(0,-1,0;1.5708rad)
  shape: bbox 0.6 x 0.5 x 0.5 mm, 6 faces (baked)
FEATURE [Part::Feature] Part__Feature114  label="SMD Capacitor, Configurable, Raspberry Pi Pico-R3_C053"
  Placement = pos=(-4.7,0.5,-3.1) rot=(0,-1,0;1.5708rad)
  shape: bbox 0.2 x 0.5 x 0.5 mm, 6 faces (baked)
FEATURE [Part::Feature] Part__Feature115  label="SMD Capacitor, Configurable, Raspberry Pi Pico-R3_C054"
  Placement = pos=(-4.7,0.5,-3.1) rot=(0,-1,0;1.5708rad)
  shape: bbox 0.2 x 0.5 x 0.5 mm, 6 faces (baked)
FEATURE [App::Part] SMD_Capacitor__Configurable__Raspberry_Pi_Pico_R3_C18  label="SMD Capacitor, Configurable, Raspberry Pi Pico-R3_C055"
  Group = -> [Part__Feature113,Part__Feature114,Part__Feature115]
  Origin = -> Origin041
FEATURE [App::Part] Raspberry_Pi_Pico_R3  label="U1_Raspberry Pi Pico-R3_b0c0d550278d"
  Group = -> [Part__Feature,MicroUSB_Port__Raspberry_Pi_Pico_R3,Part__Feature008,Part__Feature009,Part__Feature010,Part__Feature011,Part__Feature012,Part__Feature013,Part__Feature014,Part__Feature015,Part__Feature016,SMD_Resistor__Configurable__Raspberry_Pi_Pico_R3_R1,SMD_Resistor__Configurable__Raspberry_Pi_Pico_R3_R2,SMD_Resistor__Configurable__Raspberry_Pi_Pico_R3_R3,+30 more]
  Origin = -> Origin042
  Placement = pos=(0,59.8,0.5) rot=(1,0,0;1.5708rad)
FEATURE [Part::Feature] Shape003  label="J5_PinHeader_1x02_P254mm_Horizontal_238d1df2211d"
  Placement = pos=(44.953,49.075,0) rot=(0,0,1;1.5708rad)
  shape: bbox 5.08 x 10.36 x 5.54 mm, 58 faces (baked)
FEATURE [App::Link] R33_R_0603_1608Metric_b52117b7a5b0_ln_007  label="R39_R_0603_1608Metric_3a9fc06c5b45"
  LinkPlacement = pos=(16.955,59.038,0) rot=(0,0,1;3.14159rad)
  LinkedObject = -> Shape
  Placement = pos=(16.955,59.038,0) rot=(0,0,1;3.14159rad)
FEATURE [Part::Feature] Shape004  label="D2_D_MiniMELF_Standard_66865c6f3843"
  Placement = pos=(-16.89,76.31,0) rot=(0,0,1;0rad)
  shape: bbox 3.6 x 1.4 x 1.4 mm, 13 faces (baked)
FEATURE [App::Link] D2_D_MiniMELF_Standard_66865c6f3843_ln_  label="D3_D_MiniMELF_Standard_57fc90e5e8b8"
  LinkPlacement = pos=(25.21,41.865,0) rot=(0,0,1;1.5708rad)
  LinkedObject = -> Shape004
  Placement = pos=(25.21,41.865,0) rot=(0,0,1;1.5708rad)
FEATURE [App::Link] C18_C_0805_2012Metric_1ea8b0f87ad5_ln_  label="C19_C_0805_2012Metric_9693c4f7710b"
  LinkPlacement = pos=(16.51,67.42,0) rot=(0,0,1;1.5708rad)
  LinkedObject = -> Shape002
  Placement = pos=(16.51,67.42,0) rot=(0,0,1;1.5708rad)
FEATURE [App::Link] R33_R_0603_1608Metric_b52117b7a5b0_ln_008  label="R7_R_0603_1608Metric_a9e5536e4d5f"
  LinkPlacement = pos=(-11.43,21.51,0) rot=(0,0,1;1.5708rad)
  LinkedObject = -> Shape
  Placement = pos=(-11.43,21.51,0) rot=(0,0,1;1.5708rad)
FEATURE [Part::Feature] Shape005  label="Q1_SOT_23_a91f0ad9a54d"
  Placement = pos=(-17.78,80.4525,0) rot=(0,0,-1;1.5708rad)
  shape: bbox 3 x 2.5 x 1.2 mm, 76 faces (baked)
FEATURE [Part::Feature] Part__Feature116  label="Lump_2"
  shape: bbox 9.5 x 9.5 x 1 mm, 1 faces, 0 solids (baked)
FEATURE [Part::Feature] Part__Feature117  label="Lump_003"
  shape: bbox 7.5 x 7.5 x 2e-07 mm, 1 faces, 0 solids (baked)
FEATURE [Part::Feature] Part__Feature118  label="Lump_004"
  shape: bbox 9.5 x 9.5 x 1.025 mm, 1 faces, 0 solids (baked)
FEATURE [Part::Feature] Part__Feature119  label="Lump_005"
  shape: bbox 0.4 x 1.3 x 1.3 mm, 1 faces, 0 solids (baked)
FEATURE [Part::Feature] Part__Feature120  label="Lump_006"
  shape: bbox 0.4 x 1.3 x 1.3 mm, 1 faces, 0 solids (baked)
FEATURE [Part::Feature] Part__Feature121  label="Lump_007"
  shape: bbox 2e-07 x 2.2 x 5.7 mm, 1 faces, 0 solids (baked)
FEATURE [Part::Feature] Part__Feature122  label="Lump_008"
  shape: bbox 0.4 x 2.2 x 1.1 mm, 1 faces, 0 solids (baked)
FEATURE [Part::Feature] Part__Feature123  label="Lump_009"
  shape: bbox 2e-07 x 2.2 x 5.7 mm, 1 faces, 0 solids (baked)
FEATURE [Part::Feature] Part__Feature124  label="Lump_010"
  shape: bbox 0.4 x 2.2 x 1.1 mm, 1 faces, 0 solids (baked)
FEATURE [Part::Feature] Part__Feature125  label="Lump_011"
  shape: bbox 2e-07 x 2.2 x 5.7 mm, 1 faces, 0 solids (baked)
FEATURE [Part::Feature] Part__Feature126  label="Lump_012"
  shape: bbox 0.4 x 2e-07 x 4.6 mm, 1 faces, 0 solids (baked)
FEATURE [Part::Feature] Part__Feature127  label="Lump_013"
  shape: bbox 0.4 x 2e-07 x 4.6 mm, 1 faces, 0 solids (baked)
FEATURE [Part::Feature] Part__Feature128  label="Lump_014"
  shape: bbox 2e-07 x 2.2 x 5.7 mm, 1 faces, 0 solids (baked)
FEATURE [Part::Feature] Part__Feature129  label="Lump_015"
  shape: bbox 0.4 x 2e-07 x 4.6 mm, 1 faces, 0 solids (baked)
FEATURE [Part::Feature] Part__Feature130  label="Lump_016"
  shape: bbox 0.4 x 2e-07 x 4.6 mm, 1 faces, 0 solids (baked)
FEATURE [Part::Feature] Part__Feature131  label="Lump_017"
  shape: bbox 7 x 7 x 5.4 mm, 1 faces, 0 solids (baked)
FEATURE [Part::Feature] Part__Feature132  label="Lump_018"
  shape: bbox 6 x 6 x 2e-07 mm, 1 faces, 0 solids (baked)
FEATURE [Part::Feature] Part__Feature133  label="Lump_019"
  shape: bbox 6 x 6 x 3.8 mm, 1 faces, 0 solids (baked)
FEATURE [Part::Feature] Part__Feature134  label="Lump_020"
  shape: bbox 6 x 6 x 2e-07 mm, 1 faces, 0 solids (baked)
FEATURE [Part::Feature] Part__Feature135  label="Lump_021"
  shape: bbox 4.8 x 4.8 x 3 mm, 1 faces, 0 solids (baked)
FEATURE [Part::Feature] Part__Feature136  label="Lump_022"
  shape: bbox 9.5 x 9.5 x 2e-07 mm, 1 faces, 0 solids (baked)
FEATURE [Part::Feature] Part__Feature137  label="Lump_023"
  shape: bbox 7.2 x 7.2 x 6 mm, 1 faces, 0 solids (baked)
FEATURE [Part::Feature] Part__Feature138  label="Lump_024"
  shape: bbox 7.2 x 7.2 x 2e-07 mm, 1 faces, 0 solids (baked)
FEATURE [Part::Feature] Part__Feature139  label="Face_312"
  shape: bbox 4.8 x 4.8 x 2.4 mm, 1 faces, 0 solids (baked)
FEATURE [Part::Feature] Part__Feature140  label="Face_313"
  shape: bbox 5.9 x 5.9 x 0.55 mm, 1 faces, 0 solids (baked)
FEATURE [App::Part] pbs_10_button  label="SW2_pbs-10-button_4ad3c1370bd2[2]"
  Group = -> [Part__Feature116,Part__Feature117,Part__Feature118,Part__Feature119,Part__Feature120,Part__Feature121,Part__Feature122,Part__Feature123,Part__Feature124,Part__Feature125,Part__Feature126,Part__Feature127,Part__Feature128,Part__Feature129,Part__Feature130,Part__Feature131,Part__Feature132,Part__Feature133,Part__Feature134,Part__Feature135,Part__Feature136,Part__Feature137,Part__Feature138,+2 more]
  Origin = -> Origin043
  Placement = pos=(-35,39,0) rot=(0,0,1;1.5708rad)
FEATURE [App::Link] R33_R_0603_1608Metric_b52117b7a5b0_ln_009  label="R14_R_0603_1608Metric_f3c93fddb9cf"
  LinkPlacement = pos=(-3.81,13.89,0) rot=(0,0,-1;1.5708rad)
  LinkedObject = -> Shape
  Placement = pos=(-3.81,13.89,0) rot=(0,0,-1;1.5708rad)
FEATURE [App::Link] R33_R_0603_1608Metric_b52117b7a5b0_ln_010  label="R34_R_0603_1608Metric_14b4b50726c8"
  LinkPlacement = pos=(-19.05,72.945,0) rot=(0,0,-1;1.5708rad)
  LinkedObject = -> Shape
  Placement = pos=(-19.05,72.945,0) rot=(0,0,-1;1.5708rad)
FEATURE [App::Link] R33_R_0603_1608Metric_b52117b7a5b0_ln_011  label="R10_R_0603_1608Metric_97d92fc8e86c"
  LinkPlacement = pos=(-8.89,13.89,0) rot=(0,0,-1;1.5708rad)
  LinkedObject = -> Shape
  Placement = pos=(-8.89,13.89,0) rot=(0,0,-1;1.5708rad)
FEATURE [App::Link] C5_C_0603_1608Metric_656f8ebd2c8c_ln_001  label="C15_C_0603_1608Metric_55a52ef95c86"
  LinkPlacement = pos=(16.51,17.65,0) rot=(0,0,-1;1.5708rad)
  LinkedObject = -> Shape001
  Placement = pos=(16.51,17.65,0) rot=(0,0,-1;1.5708rad)
FEATURE [App::Link] R33_R_0603_1608Metric_b52117b7a5b0_ln_012  label="R2_R_0603_1608Metric_f07f47fe7891"
  LinkPlacement = pos=(-19.05,13.89,0) rot=(0,0,-1;1.5708rad)
  LinkedObject = -> Shape
  Placement = pos=(-19.05,13.89,0) rot=(0,0,-1;1.5708rad)
FEATURE [App::Link] C5_C_0603_1608Metric_656f8ebd2c8c_ln_002  label="C3_C_0603_1608Metric_cd7e69ae54ee"
  LinkPlacement = pos=(-13.97,17.65,0) rot=(0,0,-1;1.5708rad)
  LinkedObject = -> Shape001
  Placement = pos=(-13.97,17.65,0) rot=(0,0,-1;1.5708rad)
FEATURE [App::Link] C5_C_0603_1608Metric_656f8ebd2c8c_ln_003  label="C10_C_0603_1608Metric_d838564a20c3"
  LinkPlacement = pos=(3.81,17.65,0) rot=(0,0,-1;1.5708rad)
  LinkedObject = -> Shape001
  Placement = pos=(3.81,17.65,0) rot=(0,0,-1;1.5708rad)
FEATURE [App::Link] R33_R_0603_1608Metric_b52117b7a5b0_ln_013  label="R3_R_0603_1608Metric_a9942397c697"
  LinkPlacement = pos=(-16.51,21.51,0) rot=(0,0,1;1.5708rad)
  LinkedObject = -> Shape
  Placement = pos=(-16.51,21.51,0) rot=(0,0,1;1.5708rad)
FEATURE [App::Link] SW2_pbs_10_button_4ad3c1370bd2_2__ln_  label="SW1_pbs-10-button_f9eef3b981e7[2]"
  LinkPlacement = pos=(-35,54,0) rot=(0,0,1;1.5708rad)
  LinkedObject = -> pbs_10_button
  Placement = pos=(-35,54,0) rot=(0,0,1;1.5708rad)
FEATURE [Part::Feature] Part__Feature141  label="DIN5_PCB_DELTRON_BODY"
  shape: bbox 21.2 x 21 x 13.6 mm, 162 faces (baked)
FEATURE [Part::Feature] Part__Feature142  label="DIN5_PCB_DELTRON_PIN2"
  Placement = pos=(-1e-15,-4,-12.5) rot=(0,0,1;0rad)
  shape: bbox 0.8 x 12.35 x 11.9 mm, 20 faces (baked)
FEATURE [Part::Feature] Part__Feature143  label="DIN5_PCB_DELTRON_PIN5"
  Placement = pos=(4e-15,-2.2e-14,-15.5) rot=(0,0,1;0rad)
  shape: bbox 3.95 x 13.4 x 13.8 mm, 24 faces (baked)
FEATURE [Part::Feature] Part__Feature144  label="DIN5_PCB_DELTRON_PIN3"
  Placement = pos=(-7.5,-4,-13.6) rot=(0,1,0;3.14159rad)
  shape: bbox 5.504 x 15.86 x 11.9 mm, 24 faces (baked)
FEATURE [Part::Feature] Part__Feature145  label="DIN5_PCB_DELTRON_PIN4"
  Placement = pos=(-1.4e-14,-3e-15,-15.5) rot=(0,1,0;3.14159rad)
  shape: bbox 3.95 x 13.4 x 13.8 mm, 24 faces (baked)
FEATURE [Part::Feature] Part__Feature146  label="DIN5_PCB_DELTRON_PIN1"
  Placement = pos=(7.5,-4,-13.6) rot=(0,0,1;0rad)
  shape: bbox 5.504 x 15.86 x 11.9 mm, 24 faces (baked)
FEATURE [Part::Feature] Part__Feature147  label="DIN5_PCB_DELTRON_FIX"
  Placement = pos=(-6.72713,43.7401,-13.4) rot=(0,0,1;0rad)
  shape: bbox 10.85 x 8.3 x 1.4 mm, 20 faces (baked)
FEATURE [Part::Feature] Part__Feature148  label="DIN5_PCB_DELTRON_SHIELD"
  Placement = pos=(-2e-15,-3.6,-2.3) rot=(0,0,1;0rad)
  shape: bbox 11.5 x 7.46 x 6.608 mm, 104 faces (baked)
FEATURE [App::Part] DIN5_PCB_DELTRON_671_0500  label="J2_DIN5_PCB_DELTRON_671-0500_992eaba440a7"
  Group = -> [Part__Feature141,Part__Feature142,Part__Feature143,Part__Feature144,Part__Feature145,Part__Feature146,Part__Feature147,Part__Feature148]
  Origin = -> Origin044
  Placement = pos=(-30.48,86.35,0) rot=(0,0.707107,0.707107;3.14159rad)
FEATURE [App::Link] R33_R_0603_1608Metric_b52117b7a5b0_ln_014  label="R38_R_0603_1608Metric_e21f65b55778"
  LinkPlacement = pos=(14.923,61.07,0) rot=(0,0,1;3.14159rad)
  LinkedObject = -> Shape
  Placement = pos=(14.923,61.07,0) rot=(0,0,1;3.14159rad)
FEATURE [App::Link] R33_R_0603_1608Metric_b52117b7a5b0_ln_015  label="R21_R_0603_1608Metric_0efd9c4b8b55"
  LinkPlacement = pos=(6.35,21.51,0) rot=(0,0,1;1.5708rad)
  LinkedObject = -> Shape
  Placement = pos=(6.35,21.51,0) rot=(0,0,1;1.5708rad)
FEATURE [App::Link] C5_C_0603_1608Metric_656f8ebd2c8c_ln_004  label="C7_C_0603_1608Metric_53fe1831df28"
  LinkPlacement = pos=(-3.81,17.65,0) rot=(0,0,-1;1.5708rad)
  LinkedObject = -> Shape001
  Placement = pos=(-3.81,17.65,0) rot=(0,0,-1;1.5708rad)
FEATURE [App::Link] R33_R_0603_1608Metric_b52117b7a5b0_ln_016  label="R24_R_0603_1608Metric_e39e0c9a5dc5"
  LinkPlacement = pos=(8.89,13.89,0) rot=(0,0,-1;1.5708rad)
  LinkedObject = -> Shape
  Placement = pos=(8.89,13.89,0) rot=(0,0,-1;1.5708rad)
FEATURE [App::Link] R33_R_0603_1608Metric_b52117b7a5b0_ln_017  label="R12_R_0603_1608Metric_2713b8e862ee"
  LinkPlacement = pos=(-6.35,13.89,0) rot=(0,0,-1;1.5708rad)
  LinkedObject = -> Shape
  Placement = pos=(-6.35,13.89,0) rot=(0,0,-1;1.5708rad)
FEATURE [App::Link] C5_C_0603_1608Metric_656f8ebd2c8c_ln_005  label="C13_C_0603_1608Metric_9b55c8525bb1"
  LinkPlacement = pos=(11.43,17.65,0) rot=(0,0,-1;1.5708rad)
  LinkedObject = -> Shape001
  Placement = pos=(11.43,17.65,0) rot=(0,0,-1;1.5708rad)
FEATURE [App::Link] R33_R_0603_1608Metric_b52117b7a5b0_ln_018  label="R36_R_0603_1608Metric_7d51529d5af5"
  LinkPlacement = pos=(20.955,43.29,0) rot=(0,0,1;0rad)
  LinkedObject = -> Shape
  Placement = pos=(20.955,43.29,0) rot=(0,0,1;0rad)
FEATURE [App::Link] C5_C_0603_1608Metric_656f8ebd2c8c_ln_006  label="C11_C_0603_1608Metric_017a6a3775af"
  LinkPlacement = pos=(6.35,17.65,0) rot=(0,0,-1;1.5708rad)
  LinkedObject = -> Shape001
  Placement = pos=(6.35,17.65,0) rot=(0,0,-1;1.5708rad)
FEATURE [App::Link] R33_R_0603_1608Metric_b52117b7a5b0_ln_019  label="R19_R_0603_1608Metric_50ad16387fed"
  LinkPlacement = pos=(3.81,21.51,0) rot=(0,0,1;1.5708rad)
  LinkedObject = -> Shape
  Placement = pos=(3.81,21.51,0) rot=(0,0,1;1.5708rad)
FEATURE [App::Link] C5_C_0603_1608Metric_656f8ebd2c8c_ln_007  label="C12_C_0603_1608Metric_629e440c61b1"
  LinkPlacement = pos=(8.89,17.65,0) rot=(0,0,-1;1.5708rad)
  LinkedObject = -> Shape001
  Placement = pos=(8.89,17.65,0) rot=(0,0,-1;1.5708rad)
FEATURE [Part::Feature] Shape006  label="J4_PinHeader_1x03_P254mm_Horizontal_b2265e9e25e6"
  Placement = pos=(25.4,35.67,0) rot=(0,0,1;0rad)
  shape: bbox 10.36 x 7.62 x 5.54 mm, 85 faces (baked)
FEATURE [App::Link] R33_R_0603_1608Metric_b52117b7a5b0_ln_020  label="R22_R_0603_1608Metric_8b5fb05b2c7e"
  LinkPlacement = pos=(6.35,13.89,0) rot=(0,0,-1;1.5708rad)
  LinkedObject = -> Shape
  Placement = pos=(6.35,13.89,0) rot=(0,0,-1;1.5708rad)
FEATURE [App::Link] C18_C_0805_2012Metric_1ea8b0f87ad5_ln_001  label="C17_C_0805_2012Metric_20b52ca9990a"
  LinkPlacement = pos=(-32.07,66.15,0) rot=(0,0,1;3.14159rad)
  LinkedObject = -> Shape002
  Placement = pos=(-32.07,66.15,0) rot=(0,0,1;3.14159rad)
FEATURE [App::Link] Q1_SOT_23_a91f0ad9a54d_ln_  label="Q2_SOT_23_0f16da0acb78"
  LinkPlacement = pos=(21.4,39.8,0) rot=(0,0,1;0rad)
  LinkedObject = -> Shape005
  Placement = pos=(21.4,39.8,0) rot=(0,0,1;0rad)
FEATURE [App::Link] R33_R_0603_1608Metric_b52117b7a5b0_ln_021  label="R20_R_0603_1608Metric_a33fdfd0a3fc"
  LinkPlacement = pos=(3.81,13.89,0) rot=(0,0,-1;1.5708rad)
  LinkedObject = -> Shape
  Placement = pos=(3.81,13.89,0) rot=(0,0,-1;1.5708rad)
FEATURE [Part::Feature] Shape007  label="D1_D_SMB_7c09f5b97a5d"
  Placement = pos=(20.32,80.014,0) rot=(0,0,-1;1.5708rad)
  shape: bbox 3.55 x 5.3 x 2.15 mm, 41 faces (baked)
FEATURE [App::Link] R33_R_0603_1608Metric_b52117b7a5b0_ln_022  label="R5_R_0603_1608Metric_9821b281269c"
  LinkPlacement = pos=(-13.97,21.51,0) rot=(0,0,1;1.5708rad)
  LinkedObject = -> Shape
  Placement = pos=(-13.97,21.51,0) rot=(0,0,1;1.5708rad)
FEATURE [App::Link] R33_R_0603_1608Metric_b52117b7a5b0_ln_023  label="R9_R_0603_1608Metric_fd4ee968c86f"
  LinkPlacement = pos=(-8.89,21.51,0) rot=(0,0,1;1.5708rad)
  LinkedObject = -> Shape
  Placement = pos=(-8.89,21.51,0) rot=(0,0,1;1.5708rad)
FEATURE [App::Link] C5_C_0603_1608Metric_656f8ebd2c8c_ln_008  label="C4_C_0603_1608Metric_6f686bac2190"
  LinkPlacement = pos=(-11.43,17.65,0) rot=(0,0,-1;1.5708rad)
  LinkedObject = -> Shape001
  Placement = pos=(-11.43,17.65,0) rot=(0,0,-1;1.5708rad)
FEATURE [App::Link] R33_R_0603_1608Metric_b52117b7a5b0_ln_024  label="R16_R_0603_1608Metric_033382074aca"
  LinkPlacement = pos=(-1.27,13.89,0) rot=(0,0,-1;1.5708rad)
  LinkedObject = -> Shape
  Placement = pos=(-1.27,13.89,0) rot=(0,0,-1;1.5708rad)
FEATURE [App::Link] C5_C_0603_1608Metric_656f8ebd2c8c_ln_009  label="C14_C_0603_1608Metric_38f74b42e5ca"
  LinkPlacement = pos=(13.97,17.65,0) rot=(0,0,-1;1.5708rad)
  LinkedObject = -> Shape001
  Placement = pos=(13.97,17.65,0) rot=(0,0,-1;1.5708rad)
FEATURE [App::Link] R33_R_0603_1608Metric_b52117b7a5b0_ln_025  label="R31_R_0603_1608Metric_d9d34907ce3c"
  LinkPlacement = pos=(19.05,21.51,0) rot=(0,0,1;1.5708rad)
  LinkedObject = -> Shape
  Placement = pos=(19.05,21.51,0) rot=(0,0,1;1.5708rad)
FEATURE [App::Link] C5_C_0603_1608Metric_656f8ebd2c8c_ln_010  label="C9_C_0603_1608Metric_d5a388dd6449"
  LinkPlacement = pos=(1.27,17.65,0) rot=(0,0,-1;1.5708rad)
  LinkedObject = -> Shape001
  Placement = pos=(1.27,17.65,0) rot=(0,0,-1;1.5708rad)
FEATURE [App::Link] R33_R_0603_1608Metric_b52117b7a5b0_ln_026  label="R37_R_0603_1608Metric_d50acf6225f6"
  LinkPlacement = pos=(21.59,31.415,0) rot=(0,0,-1;1.5708rad)
  LinkedObject = -> Shape
  Placement = pos=(21.59,31.415,0) rot=(0,0,-1;1.5708rad)
FEATURE [App::Link] R33_R_0603_1608Metric_b52117b7a5b0_ln_027  label="R6_R_0603_1608Metric_5e1a482a6bf2"
  LinkPlacement = pos=(-13.97,13.89,0) rot=(0,0,-1;1.5708rad)
  LinkedObject = -> Shape
  Placement = pos=(-13.97,13.89,0) rot=(0,0,-1;1.5708rad)
FEATURE [App::Link] R33_R_0603_1608Metric_b52117b7a5b0_ln_028  label="R27_R_0603_1608Metric_bc561b712ee3"
  LinkPlacement = pos=(13.97,21.51,0) rot=(0,0,1;1.5708rad)
  LinkedObject = -> Shape
  Placement = pos=(13.97,21.51,0) rot=(0,0,1;1.5708rad)
FEATURE [App::Link] R33_R_0603_1608Metric_b52117b7a5b0_ln_029  label="R28_R_0603_1608Metric_6bced3f87a0c"
  LinkPlacement = pos=(13.97,13.89,0) rot=(0,0,-1;1.5708rad)
  LinkedObject = -> Shape
  Placement = pos=(13.97,13.89,0) rot=(0,0,-1;1.5708rad)
FEATURE [App::Link] C5_C_0603_1608Metric_656f8ebd2c8c_ln_011  label="C16_C_0603_1608Metric_c61538164557"
  LinkPlacement = pos=(19.05,17.65,0) rot=(0,0,-1;1.5708rad)
  LinkedObject = -> Shape001
  Placement = pos=(19.05,17.65,0) rot=(0,0,-1;1.5708rad)
FEATURE [App::Link] R33_R_0603_1608Metric_b52117b7a5b0_ln_030  label="R15_R_0603_1608Metric_e4c3380dd029"
  LinkPlacement = pos=(-1.27,21.51,0) rot=(0,0,1;1.5708rad)
  LinkedObject = -> Shape
  Placement = pos=(-1.27,21.51,0) rot=(0,0,1;1.5708rad)
FEATURE [App::Link] R33_R_0603_1608Metric_b52117b7a5b0_ln_031  label="R1_R_0603_1608Metric_7f6011f865b7"
  LinkPlacement = pos=(-19.05,21.51,0) rot=(0,0,1;1.5708rad)
  LinkedObject = -> Shape
  Placement = pos=(-19.05,21.51,0) rot=(0,0,1;1.5708rad)
FEATURE [Part::Feature] Part__Feature149  label="R0904N-L-25KQ"
  shape: bbox 11.4 x 12.65 x 11.7 mm, 202 faces (baked)
FEATURE [Part::Feature] Part__Feature150  label="R0904N-L-25KQ001"
  shape: bbox 6.059 x 6.059 x 17.11 mm, 130 faces (baked)
FEATURE [App::Part] R0904N_L_25KQ  label="RV1_R0904N-L-25KQ002_d2b4d1234d3a"
  Group = -> [Part__Feature149,Part__Feature150]
  Origin = -> Origin045
  Placement = pos=(35,54,0) rot=(0,0,-1;1.5708rad)
FEATURE [App::Link] R33_R_0603_1608Metric_b52117b7a5b0_ln_032  label="R32_R_0603_1608Metric_6ff04160d3cc"
  LinkPlacement = pos=(19.05,13.89,0) rot=(0,0,-1;1.5708rad)
  LinkedObject = -> Shape
  Placement = pos=(19.05,13.89,0) rot=(0,0,-1;1.5708rad)
FEATURE [App::Link] C5_C_0603_1608Metric_656f8ebd2c8c_ln_012  label="C6_C_0603_1608Metric_bbe526463624"
  LinkPlacement = pos=(-6.35,17.65,0) rot=(0,0,-1;1.5708rad)
  LinkedObject = -> Shape001
  Placement = pos=(-6.35,17.65,0) rot=(0,0,-1;1.5708rad)
FEATURE [App::Link] R33_R_0603_1608Metric_b52117b7a5b0_ln_033  label="R23_R_0603_1608Metric_8471ef869ea4"
  LinkPlacement = pos=(8.89,21.51,0) rot=(0,0,1;1.5708rad)
  LinkedObject = -> Shape
  Placement = pos=(8.89,21.51,0) rot=(0,0,1;1.5708rad)
FEATURE [App::Link] R33_R_0603_1608Metric_b52117b7a5b0_ln_034  label="R30_R_0603_1608Metric_3d78b7460ece"
  LinkPlacement = pos=(16.51,13.89,0) rot=(0,0,-1;1.5708rad)
  LinkedObject = -> Shape
  Placement = pos=(16.51,13.89,0) rot=(0,0,-1;1.5708rad)
FEATURE [App::Link] R33_R_0603_1608Metric_b52117b7a5b0_ln_035  label="R25_R_0603_1608Metric_8b5d0f6e3375"
  LinkPlacement = pos=(11.43,21.51,0) rot=(0,0,1;1.5708rad)
  LinkedObject = -> Shape
  Placement = pos=(11.43,21.51,0) rot=(0,0,1;1.5708rad)
FEATURE [App::Link] R33_R_0603_1608Metric_b52117b7a5b0_ln_036  label="R4_R_0603_1608Metric_829a3774e3c8"
  LinkPlacement = pos=(-16.51,13.89,0) rot=(0,0,-1;1.5708rad)
  LinkedObject = -> Shape
  Placement = pos=(-16.51,13.89,0) rot=(0,0,-1;1.5708rad)
FEATURE [Part::Feature] Shape008  label="J1_PinHeader_2x20_P254mm_Horizontal_104821f7cdcd"
  Placement = pos=(24.13,10.27,0) rot=(0,0,-1;1.5708rad)
  shape: bbox 50.8 x 12.9 x 8.08 mm, 964 faces (baked)
FEATURE [App::Link] R33_R_0603_1608Metric_b52117b7a5b0_ln_037  label="R11_R_0603_1608Metric_53abc7938dfc"
  LinkPlacement = pos=(-6.35,21.51,0) rot=(0,0,1;1.5708rad)
  LinkedObject = -> Shape
  Placement = pos=(-6.35,21.51,0) rot=(0,0,1;1.5708rad)
FEATURE [App::Link] C5_C_0603_1608Metric_656f8ebd2c8c_ln_013  label="C2_C_0603_1608Metric_6790d0bcb4e1"
  LinkPlacement = pos=(-16.51,17.65,0) rot=(0,0,-1;1.5708rad)
  LinkedObject = -> Shape001
  Placement = pos=(-16.51,17.65,0) rot=(0,0,-1;1.5708rad)
FEATURE [App::Link] C5_C_0603_1608Metric_656f8ebd2c8c_ln_014  label="C8_C_0603_1608Metric_fdd8acdb4a6e"
  LinkPlacement = pos=(-1.27,17.65,0) rot=(0,0,-1;1.5708rad)
  LinkedObject = -> Shape001
  Placement = pos=(-1.27,17.65,0) rot=(0,0,-1;1.5708rad)
FEATURE [App::Part] Top_1056
  Group = -> [Shape,Shape001,C5_C_0603_1608Metric_656f8ebd2c8c_ln_,R33_R_0603_1608Metric_b52117b7a5b0_ln_,R33_R_0603_1608Metric_b52117b7a5b0_ln_001,R33_R_0603_1608Metric_b52117b7a5b0_ln_002,Shape002,R33_R_0603_1608Metric_b52117b7a5b0_ln_003,R33_R_0603_1608Metric_b52117b7a5b0_ln_004,R33_R_0603_1608Metric_b52117b7a5b0_ln_005,R33_R_0603_1608Metric_b52117b7a5b0_ln_006,Raspberry_Pi_Pico_R3,Shape003,+58 more]
  Origin = -> Origin003
FEATURE [App::Part] Step_Models_1056
  Group = -> [Top_1056]
  Origin = -> Origin002
FEATURE [PartDesign::CoordinateSystem] Hole1
  AttacherType = Attacher::AttachEngine3D
  MapMode = 11
  Placement = pos=(-45,81,-1.6) rot=(0,0,1;1.5708rad)
  Support = -> [Pcb_1056]
FEATURE [PartDesign::CoordinateSystem] Hole2
  AttacherType = Attacher::AttachEngine3D
  MapMode = 11
  Placement = pos=(45,81,-1.6) rot=(0,0,1;1.5708rad)
  Support = -> [Pcb_1056]
FEATURE [PartDesign::CoordinateSystem] Hole3
  AttacherType = Attacher::AttachEngine3D
  MapMode = 11
  Placement = pos=(-30,9,-1.6) rot=(0,0,1;1.5708rad)
  Support = -> [Pcb_1056]
FEATURE [PartDesign::CoordinateSystem] Hole4
  AttacherType = Attacher::AttachEngine3D
  MapMode = 11
  Placement = pos=(30,9,-1.6) rot=(0,0,1;1.5708rad)
  Support = -> [Pcb_1056]
FEATURE [App::Part] Board_1056  label="touch_keyboard"
  Group = -> [Local_CS_1056,Board_Geoms_1056,Step_Models_1056,Hole1,Hole2,Hole3,Hole4]
  Origin = -> Origin001
